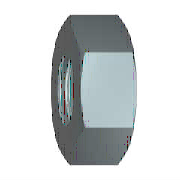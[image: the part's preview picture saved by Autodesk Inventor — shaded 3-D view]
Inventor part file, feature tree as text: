
AUTODESK INVENTOR PART (.ipt)
format: ipt  version: 2022 (Build 260153000, 153)  size: 164,864 bytes
history: native  units: mm (DEFAULTED — no unit token found)
features: sketch x3, other x2, extrude x1, hole x1, plane x1
ambient origin geometry x7: Origin, YZ Plane, XZ Plane, X Axis, Y Axis, Z Axis, Center Point
bodies: Solid1 (feature_tree)
feature tree (8):
  extrude  "Базовый элемент"  Depth=15.011107mm
  other  "Фаска1"
  hole  "Резьба"  [1 undecoded]
  other  "Work Axis1"
  plane  "Work Plane1"
  sketch  "Эскиз1"
  sketch  "Эскиз2"
  sketch  "Эскиз3"
note: 1 required parameter value undecoded (feature->parameter linkage not recoverable at this tier; creation-order binding heuristic only, values carry confidence <= 0.55)
